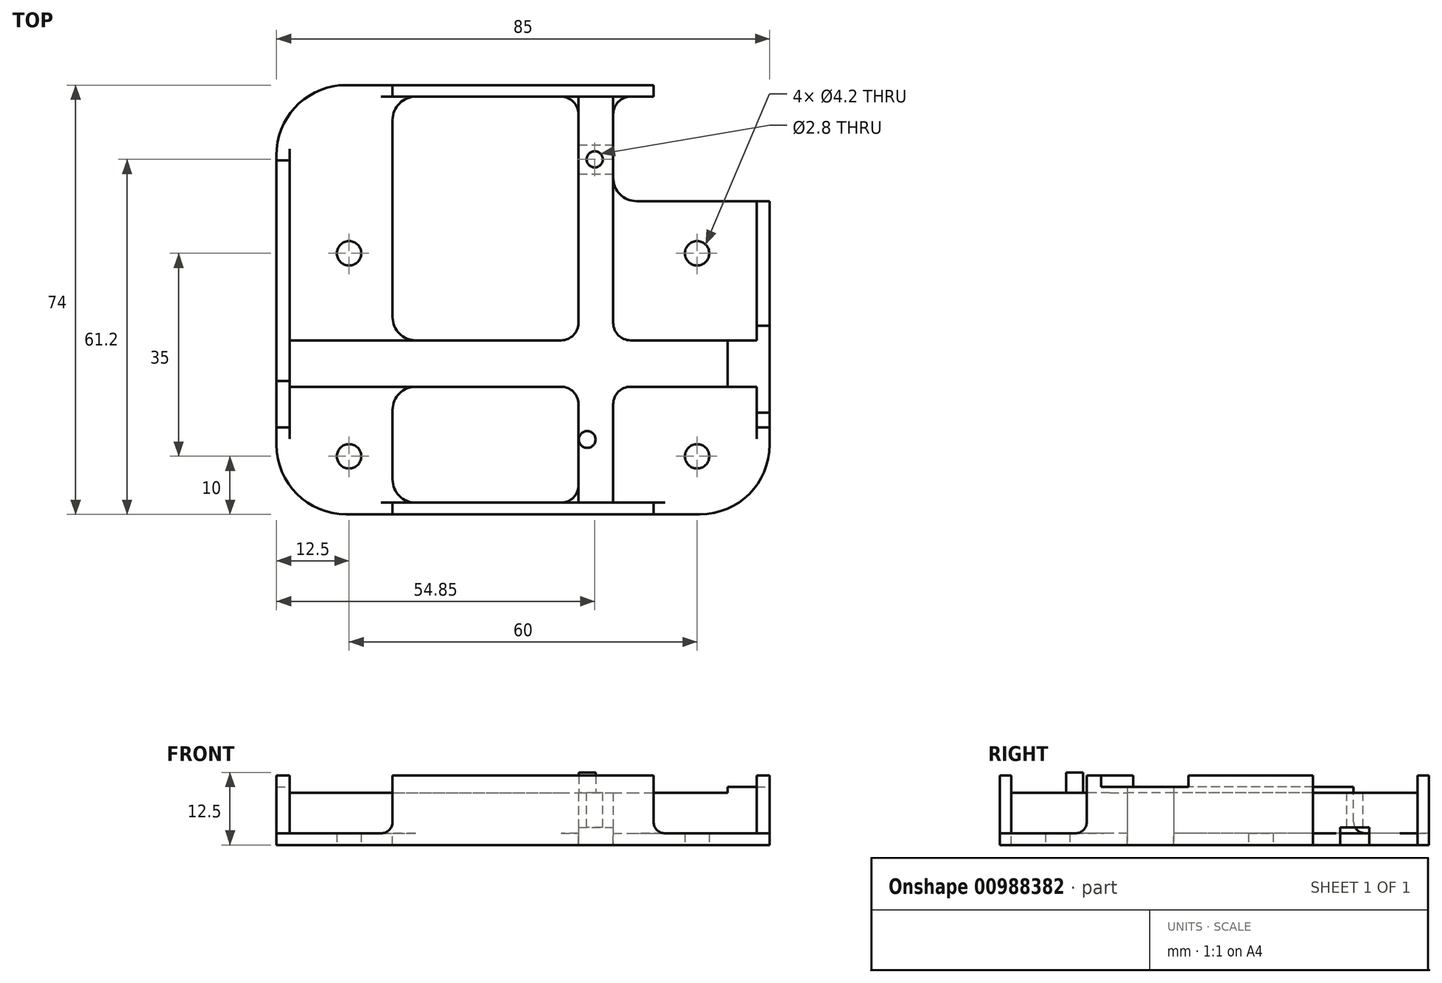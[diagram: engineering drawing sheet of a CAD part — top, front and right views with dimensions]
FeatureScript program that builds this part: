
annotation { "Feature Type Name" : "Feature", "Feature Type Description" : "" }
export const myFeature = defineFeature(function(context is Context, id is Id, definition is map)
    precondition{}
    {
        {
            var Q0;
            Q0=qCreatedBy(makeId("Top.planeOp"),FACE);
            var sketch = newSketch(context, id + "F0", { "sketchPlane" : qUnion([Q0])});
            skLineSegment(sketch, "E0.bottom", {"start": v(-42.5, 37) * mm, "end": v(42.5, 37) * mm});
            skLineSegment(sketch, "E0.top", {"start": v(-42.5, -37) * mm, "end": v(42.5, -37) * mm});
            skLineSegment(sketch, "E0.left", {"start": v(-42.5, 37) * mm, "end": v(-42.5, -37) * mm});
            skLineSegment(sketch, "E0.right", {"start": v(42.5, 37) * mm, "end": v(42.5, -37) * mm});
            skCircle(sketch, "E1", {"center": v(-30, 8) * mm, "radius": 2.1 * mm});
            skCircle(sketch, "E2", {"center": v(30, 8) * mm, "radius": 2.1 * mm});
            skCircle(sketch, "E3", {"center": v(30, -27) * mm, "radius": 2.1 * mm});
            skCircle(sketch, "E4", {"center": v(-30, -27) * mm, "radius": 2.1 * mm});
            skLineSegment(sketch, "E5.bottom", {"start": v(-30, 8) * mm, "end": v(30, 8) * mm, "construction": true});
            skLineSegment(sketch, "E5.top", {"start": v(-30, -27) * mm, "end": v(30, -27) * mm, "construction": true});
            skLineSegment(sketch, "E5.left", {"start": v(-30, 8) * mm, "end": v(-30, -27) * mm, "construction": true});
            skLineSegment(sketch, "E5.right", {"start": v(30, 8) * mm, "end": v(30, -27) * mm, "construction": true});
            skPoint(sketch, "E6", {"position": v(0, 8) * mm});
            skPoint(sketch, "E7", {"position": v(30, -9.5) * mm});
            skPoint(sketch, "E8", {"position": v(0, 37) * mm});
            skPoint(sketch, "E9", {"position": v(42.5, 0) * mm});
            skSolve(sketch);
        }
        {
            var Q0;
            Q0=makeQuery(id+"F0.imprint","IMPRINT",FACE,{"disambiguationData":[TD([[makeQuery(id+"F0.imprint","IMPRINT",EDGE,{"derivedFrom":sQuery(id+"F0.wireOp",EDGE,"E0.bottom")}),-1.0]])]});
            extrude(context, id + "F1", {"entities" : qUnion([Q0]), "depth" : 12 * mm, "offsetDistance" : 25 * mm});
        }
        {
            var Q0;
            Q0=makeQuery(id+"F1.opExtrude","CAP_FACE",FACE,{"disambiguationData":[OSD([sQuery(id+"F0.wireOp",EDGE,"E0.bottom"),sQuery(id+"F0.wireOp",EDGE,"E0.top"),sQuery(id+"F0.wireOp",EDGE,"E0.left"),sQuery(id+"F0.wireOp",EDGE,"E0.right"),sQuery(id+"F0.wireOp",EDGE,"E1"),sQuery(id+"F0.wireOp",EDGE,"E2"),sQuery(id+"F0.wireOp",EDGE,"E3"),sQuery(id+"F0.wireOp",EDGE,"E4")])],"isStart":false});
            var sketch = newSketch(context, id + "F2", { "sketchPlane" : qUnion([Q0])});
            skLineSegment(sketch, "E10.bottom", {"start": v(-40.25, 35) * mm, "end": v(40.25, 35) * mm});
            skLineSegment(sketch, "E10.top", {"start": v(-40.25, -35) * mm, "end": v(40.25, -35) * mm});
            skLineSegment(sketch, "E10.left", {"start": v(-40.25, 35) * mm, "end": v(-40.25, -35) * mm});
            skLineSegment(sketch, "E10.right", {"start": v(40.25, 35) * mm, "end": v(40.25, -35) * mm});
            skPoint(sketch, "E11", {"position": v(0, 35) * mm});
            skPoint(sketch, "E12", {"position": v(40.25, 0) * mm});
            skSolve(sketch);
        }
        {
            var Q0;
            Q0=makeQuery(id+"F2.imprint","IMPRINT",FACE,{"disambiguationData":[TD([[makeQuery(id+"F2.imprint","IMPRINT",EDGE,{"derivedFrom":sQuery(id+"F2.wireOp",EDGE,"E10.bottom")}),-1.0]])]});
            extrude(context, id + "F3", {"entities" : qUnion([Q0]), "operationType" : NewBodyOperationType.REMOVE, "oppositeDirection" : true, "depth" : 10 * mm, "offsetDistance" : 25 * mm});
        }
        {
            var Q0;
            Q0=makeQuery(id+"F3.boolean.opBoolean","COPY",FACE,{"derivedFrom":makeQuery(id+"F3.opExtrude","CAP_FACE",FACE,{"disambiguationData":[OSD([sQuery(id+"F0.wireOp",EDGE,"E1"),sQuery(id+"F0.wireOp",EDGE,"E2"),sQuery(id+"F0.wireOp",EDGE,"E3"),sQuery(id+"F0.wireOp",EDGE,"E4"),sQuery(id+"F2.wireOp",EDGE,"E10.bottom"),sQuery(id+"F2.wireOp",EDGE,"E10.top"),sQuery(id+"F2.wireOp",EDGE,"E10.left"),sQuery(id+"F2.wireOp",EDGE,"E10.right")])],"isStart":false})});
            var sketch = newSketch(context, id + "F4", { "sketchPlane" : qUnion([Q0])});
            skLineSegment(sketch, "E13.bottom", {"start": v(9.55, 35) * mm, "end": v(15.55, 35) * mm});
            skLineSegment(sketch, "E13.top", {"start": v(9.55, -35) * mm, "end": v(15.55, -35) * mm});
            skLineSegment(sketch, "E13.left", {"start": v(9.55, 35) * mm, "end": v(9.55, -35) * mm});
            skLineSegment(sketch, "E13.right", {"start": v(15.55, 35) * mm, "end": v(15.55, -35) * mm});
            skLineSegment(sketch, "E14.bottom", {"start": v(-40.25, -7) * mm, "end": v(40.25, -7) * mm});
            skLineSegment(sketch, "E14.top", {"start": v(-40.25, -15) * mm, "end": v(40.25, -15) * mm});
            skLineSegment(sketch, "E14.left", {"start": v(-40.25, -7) * mm, "end": v(-40.25, -15) * mm});
            skLineSegment(sketch, "E14.right", {"start": v(40.25, -7) * mm, "end": v(40.25, -15) * mm});
            skSolve(sketch);
        }
        {
            var Q0;
            Q0=makeQuery(id+"F4.imprint","IMPRINT",FACE,{"disambiguationData":[TD([[makeQuery(id+"F4.imprint","IMPRINT",EDGE,{"derivedFrom":sQuery(id+"F4.wireOp",EDGE,"E13.bottom")}),-1.0]])]});
            var Q1;
            {var subQ5=sQuery(id+"F4.wireOp",EDGE,"E14.left");Q1=makeQuery(id+"F4.imprint","IMPRINT",FACE,{"disambiguationData":[TD([[makeQuery(id+"F4.imprint","IMPRINT",EDGE,{"derivedFrom":subQ5}),1.0]])]});}
            var Q2;
            {var subQ0=sQuery(id+"F4.wireOp",EDGE,"E14.bottom");var subQ1=sQuery(id+"F4.wireOp",EDGE,"E13.left");var subQ2=makeQuery(id+"F4.imprint","INTERSECT",VERTEX,{"derivedFrom":[subQ1,subQ0]});Q2=makeQuery(id+"F4.imprint","IMPRINT",FACE,{"disambiguationData":[TD([[makeQuery(id+"F4.imprint","IMPRINT",EDGE,{"disambiguationData":[TD([[subQ2,-1.0]])],"derivedFrom":subQ1}),1.0]])]});}
            var Q3;
            {var subQ5=sQuery(id+"F4.wireOp",EDGE,"E14.right");Q3=makeQuery(id+"F4.imprint","IMPRINT",FACE,{"disambiguationData":[TD([[makeQuery(id+"F4.imprint","IMPRINT",EDGE,{"derivedFrom":subQ5}),-1.0]])]});}
            var Q4;
            {var subQ0=sQuery(id+"F4.wireOp",EDGE,"E13.top");Q4=makeQuery(id+"F4.imprint","IMPRINT",FACE,{"disambiguationData":[TD([[makeQuery(id+"F4.imprint","IMPRINT",EDGE,{"derivedFrom":subQ0}),1.0]])]});}
            extrude(context, id + "F5", {"entities" : qUnion([Q0, Q1, Q2, Q3, Q4]), "operationType" : NewBodyOperationType.ADD, "depth" : 7 * mm, "offsetDistance" : 25 * mm});
        }
        {
            var Q0;
            Q0=makeQuery(id+"F5.opExtrude","CAP_FACE",FACE,{"disambiguationData":[OSD([sQuery(id+"F4.wireOp",EDGE,"E13.bottom"),sQuery(id+"F4.wireOp",EDGE,"E13.top"),sQuery(id+"F4.wireOp",EDGE,"E13.left"),sQuery(id+"F4.wireOp",EDGE,"E13.right")])],"isStart":false});
            var sketch = newSketch(context, id + "F6", { "sketchPlane" : qUnion([Q0])});
            skCircle(sketch, "E15", {"center": v(12.35, 24.2) * mm, "radius": 1.4 * mm});
            skCircle(sketch, "E16", {"center": v(11.05, -24.1) * mm, "radius": 1.45 * mm});
            skSolve(sketch);
        }
        {
            var Q0;
            Q0=makeQuery(id+"F6.imprint","IMPRINT",FACE,{"disambiguationData":[TD([[makeQuery(id+"F6.imprint","IMPRINT",EDGE,{"derivedFrom":sQuery(id+"F6.wireOp",EDGE,"E16")}),1.0]])]});
            extrude(context, id + "F7", {"entities" : qUnion([Q0]), "operationType" : NewBodyOperationType.ADD, "depth" : 3.5 * mm, "offsetDistance" : 25 * mm});
        }
        {
            var Q0;
            Q0=makeQuery(id+"F1.opExtrude","CAP_FACE",FACE,{"disambiguationData":[OSD([sQuery(id+"F0.wireOp",EDGE,"E0.bottom"),sQuery(id+"F0.wireOp",EDGE,"E0.top"),sQuery(id+"F0.wireOp",EDGE,"E0.left"),sQuery(id+"F0.wireOp",EDGE,"E0.right"),sQuery(id+"F0.wireOp",EDGE,"E1"),sQuery(id+"F0.wireOp",EDGE,"E2"),sQuery(id+"F0.wireOp",EDGE,"E3"),sQuery(id+"F0.wireOp",EDGE,"E4")])],"isStart":false});
            var sketch = newSketch(context, id + "F8", { "sketchPlane" : qUnion([Q0])});
            skLineSegment(sketch, "E17.bottom", {"start": v(-42.5, 24) * mm, "end": v(-40.25, 24) * mm});
            skLineSegment(sketch, "E17.top", {"start": v(-42.5, -14) * mm, "end": v(-40.25, -14) * mm});
            skLineSegment(sketch, "E17.left", {"start": v(-42.5, 24) * mm, "end": v(-42.5, -14) * mm});
            skLineSegment(sketch, "E17.right", {"start": v(-40.25, 24) * mm, "end": v(-40.25, -14) * mm});
            skSolve(sketch);
        }
        {
            var Q0;
            Q0=makeQuery(id+"F8.imprint","IMPRINT",FACE,{"disambiguationData":[TD([[makeQuery(id+"F8.imprint","IMPRINT",EDGE,{"derivedFrom":sQuery(id+"F8.wireOp",EDGE,"E17.bottom")}),-1.0]])]});
            extrude(context, id + "F9", {"entities" : qUnion([Q0]), "operationType" : NewBodyOperationType.REMOVE, "oppositeDirection" : true, "depth" : 2 * mm, "offsetDistance" : 25 * mm});
        }
        {
            var Q0;
            Q0=makeQuery(id+"F1.opExtrude","CAP_FACE",FACE,{"disambiguationData":[OSD([sQuery(id+"F0.wireOp",EDGE,"E0.bottom"),sQuery(id+"F0.wireOp",EDGE,"E0.top"),sQuery(id+"F0.wireOp",EDGE,"E0.left"),sQuery(id+"F0.wireOp",EDGE,"E0.right"),sQuery(id+"F0.wireOp",EDGE,"E1"),sQuery(id+"F0.wireOp",EDGE,"E2"),sQuery(id+"F0.wireOp",EDGE,"E3"),sQuery(id+"F0.wireOp",EDGE,"E4")])],"isStart":false});
            var sketch = newSketch(context, id + "F10", { "sketchPlane" : qUnion([Q0])});
            skLineSegment(sketch, "E18", {"start": v(-42.5, 17) * mm, "end": v(-42.5, 37) * mm});
            skLineSegment(sketch, "E19", {"start": v(-42.5, 37) * mm, "end": v(-22.5, 37) * mm});
            skLineSegment(sketch, "E20", {"start": v(-22.5, 37) * mm, "end": v(-22.5, 35) * mm});
            skLineSegment(sketch, "E21", {"start": v(-22.5, 35) * mm, "end": v(-40.25, 35) * mm});
            skLineSegment(sketch, "E22", {"start": v(-40.25, 35) * mm, "end": v(-40.25, 17) * mm});
            skLineSegment(sketch, "E23", {"start": v(-40.25, 17) * mm, "end": v(-42.5, 17) * mm});
            skLineSegment(sketch, "E24", {"start": v(22.5, 37) * mm, "end": v(22.5, 35) * mm});
            skLineSegment(sketch, "E25", {"start": v(22.5, 35) * mm, "end": v(40.25, 35) * mm});
            skLineSegment(sketch, "E26", {"start": v(40.25, 35) * mm, "end": v(40.25, 17) * mm});
            skLineSegment(sketch, "E27", {"start": v(40.25, 17) * mm, "end": v(42.5, 17) * mm});
            skLineSegment(sketch, "E28", {"start": v(42.5, 17) * mm, "end": v(42.5, 37) * mm});
            skLineSegment(sketch, "E29", {"start": v(42.5, 37) * mm, "end": v(22.5, 37) * mm});
            skLineSegment(sketch, "E30", {"start": v(22.5, -35) * mm, "end": v(22.5, -37) * mm});
            skLineSegment(sketch, "E31", {"start": v(22.5, -37) * mm, "end": v(42.5, -37) * mm});
            skLineSegment(sketch, "E32", {"start": v(42.5, -37) * mm, "end": v(42.5, -22) * mm});
            skLineSegment(sketch, "E33", {"start": v(42.5, -22) * mm, "end": v(40.25, -22) * mm});
            skLineSegment(sketch, "E34", {"start": v(40.25, -22) * mm, "end": v(40.25, -35) * mm});
            skLineSegment(sketch, "E35", {"start": v(40.25, -35) * mm, "end": v(22.5, -35) * mm});
            skLineSegment(sketch, "E36", {"start": v(-42.5, -22) * mm, "end": v(-40.25, -22) * mm});
            skLineSegment(sketch, "E37", {"start": v(-40.25, -22) * mm, "end": v(-40.25, -35) * mm});
            skLineSegment(sketch, "E38", {"start": v(-40.25, -35) * mm, "end": v(-22.5, -35) * mm});
            skLineSegment(sketch, "E39", {"start": v(-22.5, -35) * mm, "end": v(-22.5, -37) * mm});
            skLineSegment(sketch, "E40", {"start": v(-22.5, -37) * mm, "end": v(-42.5, -37) * mm});
            skLineSegment(sketch, "E41", {"start": v(-42.5, -37) * mm, "end": v(-42.5, -22) * mm});
            skSolve(sketch);
        }
        {
            var Q0;
            Q0=makeQuery(id+"F10.imprint","IMPRINT",FACE,{"disambiguationData":[TD([[makeQuery(id+"F10.imprint","IMPRINT",EDGE,{"derivedFrom":sQuery(id+"F10.wireOp",EDGE,"E18")}),1.0]])]});
            var Q1;
            Q1=makeQuery(id+"F10.imprint","IMPRINT",FACE,{"disambiguationData":[TD([[makeQuery(id+"F10.imprint","IMPRINT",EDGE,{"derivedFrom":sQuery(id+"F10.wireOp",EDGE,"E24")}),1.0]])]});
            var Q2;
            Q2=makeQuery(id+"F10.imprint","IMPRINT",FACE,{"disambiguationData":[TD([[makeQuery(id+"F10.imprint","IMPRINT",EDGE,{"derivedFrom":sQuery(id+"F10.wireOp",EDGE,"E30")}),1.0]])]});
            var Q3;
            Q3=makeQuery(id+"F10.imprint","IMPRINT",FACE,{"disambiguationData":[TD([[makeQuery(id+"F10.imprint","IMPRINT",EDGE,{"derivedFrom":sQuery(id+"F10.wireOp",EDGE,"E36")}),-1.0]])]});
            var Q4;
            {var subQ0=sQuery(id+"F2.wireOp",EDGE,"E10.left");var subQ1=sQuery(id+"F2.wireOp",EDGE,"E10.bottom");var subQ5=sQuery(id+"F0.wireOp",EDGE,"E1");Q4=makeQuery(id+"F5.boolean.opBoolean","SPLIT",FACE,{"disambiguationData":[TD([makeQuery(id+"F1.opExtrude","SWEPT_FACE",FACE,{"disambiguationData":[OSD([subQ5])]})])],"derivedFrom":makeQuery(id+"F3.boolean.opBoolean","COPY",FACE,{"derivedFrom":makeQuery(id+"F3.opExtrude","CAP_FACE",FACE,{"disambiguationData":[OSD([subQ5,sQuery(id+"F0.wireOp",EDGE,"E2"),sQuery(id+"F0.wireOp",EDGE,"E3"),sQuery(id+"F0.wireOp",EDGE,"E4"),subQ1,sQuery(id+"F2.wireOp",EDGE,"E10.top"),subQ0,sQuery(id+"F2.wireOp",EDGE,"E10.right")])],"isStart":false})})});}
            extrude(context, id + "F11", {"entities" : qUnion([Q0, Q1, Q2, Q3]), "operationType" : NewBodyOperationType.REMOVE, "endBound" : BoundingType.UP_TO_SURFACE, "oppositeDirection" : true, "depth" : 25 * mm, "endBoundEntityFace" : qUnion([Q4]), "offsetDistance" : 25 * mm});
        }
        {
            var Q0;
            {var subQ0=sQuery(id+"F0.wireOp",EDGE,"E0.right");Q0=makeQuery(id+"F11.boolean.opBoolean","SPLIT",FACE,{"disambiguationData":[TD([makeQuery(id+"F1.opExtrude","SWEPT_FACE",FACE,{"disambiguationData":[OSD([subQ0])]})])],"derivedFrom":makeQuery(id+"F1.opExtrude","CAP_FACE",FACE,{"disambiguationData":[OSD([sQuery(id+"F0.wireOp",EDGE,"E0.bottom"),sQuery(id+"F0.wireOp",EDGE,"E0.top"),sQuery(id+"F0.wireOp",EDGE,"E0.left"),subQ0,sQuery(id+"F0.wireOp",EDGE,"E1"),sQuery(id+"F0.wireOp",EDGE,"E2"),sQuery(id+"F0.wireOp",EDGE,"E3"),sQuery(id+"F0.wireOp",EDGE,"E4")])],"isStart":false})});}
            var sketch = newSketch(context, id + "F12", { "sketchPlane" : qUnion([Q0])});
            skLineSegment(sketch, "E42.bottom", {"start": v(40.25, -4.5) * mm, "end": v(42.5, -4.5) * mm});
            skLineSegment(sketch, "E42.top", {"start": v(40.25, -19.5) * mm, "end": v(42.5, -19.5) * mm});
            skLineSegment(sketch, "E42.left", {"start": v(40.25, -4.5) * mm, "end": v(40.25, -19.5) * mm});
            skLineSegment(sketch, "E42.right", {"start": v(42.5, -4.5) * mm, "end": v(42.5, -19.5) * mm});
            skPoint(sketch, "E43", {"position": v(42.5, -12) * mm});
            skSolve(sketch);
        }
        {
            var Q0;
            Q0=makeQuery(id+"F12.imprint","IMPRINT",FACE,{"disambiguationData":[TD([[makeQuery(id+"F12.imprint","IMPRINT",EDGE,{"derivedFrom":sQuery(id+"F12.wireOp",EDGE,"E42.bottom")}),-1.0]])]});
            var Q1;
            Q1=makeQuery(id+"F9.boolean.opBoolean","MERGE",FACE,{"derivedFrom":[makeQuery(id+"F5.opExtrude","CAP_FACE",FACE,{"disambiguationData":[OSD([sQuery(id+"F4.wireOp",EDGE,"E13.bottom"),sQuery(id+"F4.wireOp",EDGE,"E13.top"),sQuery(id+"F4.wireOp",EDGE,"E13.left"),sQuery(id+"F4.wireOp",EDGE,"E13.right"),sQuery(id+"F4.wireOp",EDGE,"E14.bottom"),sQuery(id+"F4.wireOp",EDGE,"E14.top"),sQuery(id+"F4.wireOp",EDGE,"E14.left"),sQuery(id+"F4.wireOp",EDGE,"E14.right")])],"isStart":false})],"fromTools":[makeQuery(id+"F9.opExtrude","CAP_FACE",FACE,{"disambiguationData":[OSD([sQuery(id+"F8.wireOp",EDGE,"E17.bottom"),sQuery(id+"F8.wireOp",EDGE,"E17.top"),sQuery(id+"F8.wireOp",EDGE,"E17.left"),sQuery(id+"F8.wireOp",EDGE,"E17.right")])],"isStart":false})]});
            extrude(context, id + "F13", {"entities" : qUnion([Q0]), "operationType" : NewBodyOperationType.REMOVE, "oppositeDirection" : true, "depth" : 2 * mm, "endBoundEntityFace" : qUnion([Q1]), "offsetDistance" : 25 * mm});
        }
        {
            var Q0;
            Q0=makeQuery(id+"F1.opExtrude","SWEPT_EDGE",EDGE,{"disambiguationData":[OSD([sQuery(id+"F0.wireOp",EDGE,"E0.bottom"),sQuery(id+"F0.wireOp",EDGE,"E0.left")])]});
            var Q1;
            Q1=makeQuery(id+"F1.opExtrude","SWEPT_EDGE",EDGE,{"disambiguationData":[OSD([sQuery(id+"F0.wireOp",EDGE,"E0.top"),sQuery(id+"F0.wireOp",EDGE,"E0.left")])]});
            var Q2;
            Q2=makeQuery(id+"F1.opExtrude","SWEPT_EDGE",EDGE,{"disambiguationData":[OSD([sQuery(id+"F0.wireOp",EDGE,"E0.top"),sQuery(id+"F0.wireOp",EDGE,"E0.right")])]});
            var Q3;
            Q3=makeQuery(id+"F1.opExtrude","SWEPT_EDGE",EDGE,{"disambiguationData":[OSD([sQuery(id+"F0.wireOp",EDGE,"E0.bottom"),sQuery(id+"F0.wireOp",EDGE,"E0.right")])]});
            fillet(context, id + "F14", {"entities" : qUnion([Q0, Q1, Q2, Q3]), "radius" : 12 * mm, "tangentPropagation" : true, "allowEdgeOverflow" : false});
        }
        {
            var Q0;
            Q0=makeQuery(id+"F5.opExtrude","SWEPT_EDGE",EDGE,{"disambiguationData":[OSD([sQuery(id+"F4.wireOp",EDGE,"E13.left"),sQuery(id+"F4.wireOp",EDGE,"E14.bottom")])]});
            var Q1;
            Q1=makeQuery(id+"F5.opExtrude","SWEPT_EDGE",EDGE,{"disambiguationData":[OSD([sQuery(id+"F4.wireOp",EDGE,"E13.left"),sQuery(id+"F4.wireOp",EDGE,"E14.top")])]});
            var Q2;
            Q2=makeQuery(id+"F5.opExtrude","SWEPT_EDGE",EDGE,{"disambiguationData":[OSD([sQuery(id+"F4.wireOp",EDGE,"E13.right"),sQuery(id+"F4.wireOp",EDGE,"E14.top")])]});
            var Q3;
            Q3=makeQuery(id+"F5.opExtrude","SWEPT_EDGE",EDGE,{"disambiguationData":[OSD([sQuery(id+"F4.wireOp",EDGE,"E13.right"),sQuery(id+"F4.wireOp",EDGE,"E14.bottom")])]});
            var Q4;
            Q4=makeQuery(id+"F5.opExtrude","SWEPT_EDGE",EDGE,{"disambiguationData":[OSD([sQuery(id+"F2.wireOp",EDGE,"E10.left"),sQuery(id+"F4.wireOp",EDGE,"E14.bottom"),sQuery(id+"F4.wireOp",EDGE,"E14.left")])]});
            var Q5;
            Q5=makeQuery(id+"F5.opExtrude","SWEPT_EDGE",EDGE,{"disambiguationData":[OSD([sQuery(id+"F2.wireOp",EDGE,"E10.left"),sQuery(id+"F4.wireOp",EDGE,"E14.top"),sQuery(id+"F4.wireOp",EDGE,"E14.left")])]});
            var Q6;
            Q6=makeQuery(id+"F5.opExtrude","SWEPT_EDGE",EDGE,{"disambiguationData":[OSD([sQuery(id+"F2.wireOp",EDGE,"E10.bottom"),sQuery(id+"F4.wireOp",EDGE,"E13.bottom"),sQuery(id+"F4.wireOp",EDGE,"E13.left")])]});
            var Q7;
            Q7=makeQuery(id+"F5.opExtrude","SWEPT_EDGE",EDGE,{"disambiguationData":[OSD([sQuery(id+"F2.wireOp",EDGE,"E10.bottom"),sQuery(id+"F4.wireOp",EDGE,"E13.bottom"),sQuery(id+"F4.wireOp",EDGE,"E13.right")])]});
            var Q8;
            Q8=makeQuery(id+"F5.opExtrude","SWEPT_EDGE",EDGE,{"disambiguationData":[OSD([sQuery(id+"F2.wireOp",EDGE,"E10.top"),sQuery(id+"F4.wireOp",EDGE,"E13.top"),sQuery(id+"F4.wireOp",EDGE,"E13.left")])]});
            var Q9;
            Q9=makeQuery(id+"F5.opExtrude","SWEPT_EDGE",EDGE,{"disambiguationData":[OSD([sQuery(id+"F2.wireOp",EDGE,"E10.right"),sQuery(id+"F4.wireOp",EDGE,"E14.top"),sQuery(id+"F4.wireOp",EDGE,"E14.right")])]});
            var Q10;
            Q10=makeQuery(id+"F5.opExtrude","SWEPT_EDGE",EDGE,{"disambiguationData":[OSD([sQuery(id+"F2.wireOp",EDGE,"E10.top"),sQuery(id+"F4.wireOp",EDGE,"E13.top"),sQuery(id+"F4.wireOp",EDGE,"E13.right")])]});
            fillet(context, id + "F15", {"entities" : qUnion([Q0, Q1, Q2, Q3, Q4, Q5, Q6, Q7, Q8, Q9, Q10]), "radius" : 3 * mm, "tangentPropagation" : true, "allowEdgeOverflow" : false});
        }
        {
            var Q0;
            {var subQ1=sQuery(id+"F2.wireOp",EDGE,"E10.top");var subQ4=sQuery(id+"F2.wireOp",EDGE,"E10.left");var subQ5=sQuery(id+"F0.wireOp",EDGE,"E4");Q0=makeQuery(id+"F11.boolean.opBoolean","MERGE",FACE,{"derivedFrom":[makeQuery(id+"F5.boolean.opBoolean","SPLIT",FACE,{"disambiguationData":[TD([makeQuery(id+"F1.opExtrude","SWEPT_FACE",FACE,{"disambiguationData":[OSD([subQ5])]})])],"derivedFrom":makeQuery(id+"F3.boolean.opBoolean","COPY",FACE,{"derivedFrom":makeQuery(id+"F3.opExtrude","CAP_FACE",FACE,{"disambiguationData":[OSD([sQuery(id+"F0.wireOp",EDGE,"E1"),sQuery(id+"F0.wireOp",EDGE,"E2"),sQuery(id+"F0.wireOp",EDGE,"E3"),subQ5,sQuery(id+"F2.wireOp",EDGE,"E10.bottom"),subQ1,subQ4,sQuery(id+"F2.wireOp",EDGE,"E10.right")])],"isStart":false})})})],"fromTools":[makeQuery(id+"F11.opExtrude","CAP_FACE",FACE,{"disambiguationData":[OSD([sQuery(id+"F10.wireOp",EDGE,"E36"),sQuery(id+"F10.wireOp",EDGE,"E37"),sQuery(id+"F10.wireOp",EDGE,"E38"),sQuery(id+"F10.wireOp",EDGE,"E39"),sQuery(id+"F10.wireOp",EDGE,"E40"),sQuery(id+"F10.wireOp",EDGE,"E41")])],"isStart":false})]});}
            var sketch = newSketch(context, id + "F16", { "sketchPlane" : qUnion([Q0])});
            skLineSegment(sketch, "E44.0.0", {"start": v(6.55, -15) * mm, "end": v(-37.25, -15) * mm});
            skArc(sketch, "E44.0.1", {"start": v(-37.25, -15) * mm, "mid": v(-39.37, -15.88) * mm, "end": v(-40.25, -18) * mm});
            skLineSegment(sketch, "E44.0.2", {"start": v(-40.25, -18) * mm, "end": v(-40.25, -22) * mm});
            skLineSegment(sketch, "E44.0.3", {"start": v(-40.25, -22) * mm, "end": v(-42.5, -22) * mm});
            skLineSegment(sketch, "E44.0.4", {"start": v(-42.5, -22) * mm, "end": v(-42.5, -25) * mm});
            skArc(sketch, "E44.0.5", {"start": v(-42.5, -25) * mm, "mid": v(-38.99, -33.49) * mm, "end": v(-30.5, -37) * mm});
            skLineSegment(sketch, "E44.0.6", {"start": v(-30.5, -37) * mm, "end": v(-22.5, -37) * mm});
            skLineSegment(sketch, "E44.0.7", {"start": v(-22.5, -37) * mm, "end": v(-22.5, -35) * mm});
            skLineSegment(sketch, "E44.0.8", {"start": v(-22.5, -35) * mm, "end": v(6.55, -35) * mm});
            skArc(sketch, "E44.0.9", {"start": v(6.55, -35) * mm, "mid": v(8.67, -34.12) * mm, "end": v(9.55, -32) * mm});
            skLineSegment(sketch, "E44.0.10", {"start": v(9.55, -32) * mm, "end": v(9.55, -18) * mm});
            skArc(sketch, "E44.0.11", {"start": v(9.55, -18) * mm, "mid": v(8.67, -15.88) * mm, "end": v(6.55, -15) * mm});
            skLineSegment(sketch, "E45", {"start": v(-22.5, -35) * mm, "end": v(-22.5, -15) * mm});
            skSolve(sketch);
        }
        {
            var Q0;
            Q0=makeQuery(id+"F16.imprint","IMPRINT",FACE,{"disambiguationData":[TD([[makeQuery(id+"F16.imprint","IMPRINT",EDGE,{"derivedFrom":sQuery(id+"F16.wireOp",EDGE,"E44.0.8")}),1.0]])]});
            extrude(context, id + "F17", {"entities" : qUnion([Q0]), "operationType" : NewBodyOperationType.REMOVE, "endBound" : BoundingType.UP_TO_NEXT, "oppositeDirection" : true, "depth" : 25 * mm, "offsetDistance" : 25 * mm});
        }
        {
            var Q0;
            {var subQ0=sQuery(id+"F2.wireOp",EDGE,"E10.left");var subQ1=sQuery(id+"F2.wireOp",EDGE,"E10.bottom");var subQ5=sQuery(id+"F0.wireOp",EDGE,"E1");Q0=makeQuery(id+"F11.boolean.opBoolean","MERGE",FACE,{"derivedFrom":[makeQuery(id+"F5.boolean.opBoolean","SPLIT",FACE,{"disambiguationData":[TD([makeQuery(id+"F1.opExtrude","SWEPT_FACE",FACE,{"disambiguationData":[OSD([subQ5])]})])],"derivedFrom":makeQuery(id+"F3.boolean.opBoolean","COPY",FACE,{"derivedFrom":makeQuery(id+"F3.opExtrude","CAP_FACE",FACE,{"disambiguationData":[OSD([subQ5,sQuery(id+"F0.wireOp",EDGE,"E2"),sQuery(id+"F0.wireOp",EDGE,"E3"),sQuery(id+"F0.wireOp",EDGE,"E4"),subQ1,sQuery(id+"F2.wireOp",EDGE,"E10.top"),subQ0,sQuery(id+"F2.wireOp",EDGE,"E10.right")])],"isStart":false})})})],"fromTools":[makeQuery(id+"F11.opExtrude","CAP_FACE",FACE,{"disambiguationData":[OSD([sQuery(id+"F8.wireOp",EDGE,"E17.bottom"),sQuery(id+"F10.wireOp",EDGE,"E18"),sQuery(id+"F10.wireOp",EDGE,"E19"),sQuery(id+"F10.wireOp",EDGE,"E20"),sQuery(id+"F10.wireOp",EDGE,"E21"),sQuery(id+"F10.wireOp",EDGE,"E22")])],"isStart":false})]});}
            var sketch = newSketch(context, id + "F18", { "sketchPlane" : qUnion([Q0])});
            skLineSegment(sketch, "E46.0.0", {"start": v(-37.25, -7) * mm, "end": v(6.55, -7) * mm});
            skArc(sketch, "E46.0.1", {"start": v(6.55, -7) * mm, "mid": v(8.67, -6.12) * mm, "end": v(9.55, -4) * mm});
            skLineSegment(sketch, "E46.0.2", {"start": v(9.55, -4) * mm, "end": v(9.55, 32) * mm});
            skArc(sketch, "E46.0.3", {"start": v(9.55, 32) * mm, "mid": v(8.67, 34.12) * mm, "end": v(6.55, 35) * mm});
            skLineSegment(sketch, "E46.0.4", {"start": v(6.55, 35) * mm, "end": v(-22.5, 35) * mm});
            skLineSegment(sketch, "E46.0.5", {"start": v(-22.5, 35) * mm, "end": v(-22.5, 37) * mm});
            skLineSegment(sketch, "E46.0.6", {"start": v(-22.5, 37) * mm, "end": v(-30.5, 37) * mm});
            skArc(sketch, "E46.0.7", {"start": v(-30.5, 37) * mm, "mid": v(-38.99, 33.49) * mm, "end": v(-42.5, 25) * mm});
            skLineSegment(sketch, "E46.0.8", {"start": v(-42.5, 25) * mm, "end": v(-42.5, 24) * mm});
            skLineSegment(sketch, "E46.0.9", {"start": v(-42.5, 24) * mm, "end": v(-40.25, 24) * mm});
            skLineSegment(sketch, "E46.0.10", {"start": v(-40.25, 24) * mm, "end": v(-40.25, -4) * mm});
            skArc(sketch, "E46.0.11", {"start": v(-40.25, -4) * mm, "mid": v(-39.37, -6.12) * mm, "end": v(-37.25, -7) * mm});
            skLineSegment(sketch, "E47", {"start": v(-22.5, 35) * mm, "end": v(-22.5, -7) * mm});
            skSolve(sketch);
        }
        {
            var Q0;
            {var subQ0=sQuery(id+"F18.wireOp",EDGE,"E46.0.1");Q0=makeQuery(id+"F18.imprint","IMPRINT",FACE,{"disambiguationData":[TD([[makeQuery(id+"F18.imprint","IMPRINT",EDGE,{"derivedFrom":subQ0}),1.0]])]});}
            extrude(context, id + "F19", {"entities" : qUnion([Q0]), "operationType" : NewBodyOperationType.REMOVE, "endBound" : BoundingType.UP_TO_NEXT, "oppositeDirection" : true, "depth" : 25 * mm, "offsetDistance" : 25 * mm});
        }
        {
            var Q0;
            {var subQ1=sQuery(id+"F2.wireOp",EDGE,"E10.bottom");var subQ4=sQuery(id+"F2.wireOp",EDGE,"E10.right");var subQ5=sQuery(id+"F0.wireOp",EDGE,"E2");Q0=makeQuery(id+"F11.boolean.opBoolean","MERGE",FACE,{"derivedFrom":[makeQuery(id+"F5.boolean.opBoolean","SPLIT",FACE,{"disambiguationData":[TD([makeQuery(id+"F1.opExtrude","SWEPT_FACE",FACE,{"disambiguationData":[OSD([subQ5])]})])],"derivedFrom":makeQuery(id+"F3.boolean.opBoolean","COPY",FACE,{"derivedFrom":makeQuery(id+"F3.opExtrude","CAP_FACE",FACE,{"disambiguationData":[OSD([sQuery(id+"F0.wireOp",EDGE,"E1"),subQ5,sQuery(id+"F0.wireOp",EDGE,"E3"),sQuery(id+"F0.wireOp",EDGE,"E4"),subQ1,sQuery(id+"F2.wireOp",EDGE,"E10.top"),sQuery(id+"F2.wireOp",EDGE,"E10.left"),subQ4])],"isStart":false})})})],"fromTools":[makeQuery(id+"F11.opExtrude","CAP_FACE",FACE,{"disambiguationData":[OSD([sQuery(id+"F10.wireOp",EDGE,"E24"),sQuery(id+"F10.wireOp",EDGE,"E25"),sQuery(id+"F10.wireOp",EDGE,"E26"),sQuery(id+"F10.wireOp",EDGE,"E27"),sQuery(id+"F10.wireOp",EDGE,"E28"),sQuery(id+"F10.wireOp",EDGE,"E29")])],"isStart":false})]});}
            var sketch = newSketch(context, id + "F20", { "sketchPlane" : qUnion([Q0])});
            skLineSegment(sketch, "E48.0.0", {"start": v(15.55, 32) * mm, "end": v(15.55, -4) * mm});
            skArc(sketch, "E48.0.1", {"start": v(15.55, -4) * mm, "mid": v(16.43, -6.12) * mm, "end": v(18.55, -7) * mm});
            skLineSegment(sketch, "E48.0.2", {"start": v(18.55, -7) * mm, "end": v(40.25, -7) * mm});
            skLineSegment(sketch, "E48.0.3", {"start": v(40.25, -7) * mm, "end": v(40.25, 17) * mm});
            skLineSegment(sketch, "E48.0.4", {"start": v(40.25, 17) * mm, "end": v(42.5, 17) * mm});
            skLineSegment(sketch, "E48.0.5", {"start": v(42.5, 17) * mm, "end": v(42.5, 25) * mm});
            skArc(sketch, "E48.0.6", {"start": v(42.5, 25) * mm, "mid": v(38.99, 33.49) * mm, "end": v(30.5, 37) * mm});
            skLineSegment(sketch, "E48.0.7", {"start": v(30.5, 37) * mm, "end": v(22.5, 37) * mm});
            skLineSegment(sketch, "E48.0.8", {"start": v(22.5, 37) * mm, "end": v(22.5, 35) * mm});
            skLineSegment(sketch, "E48.0.9", {"start": v(22.5, 35) * mm, "end": v(18.55, 35) * mm});
            skArc(sketch, "E48.0.10", {"start": v(18.55, 35) * mm, "mid": v(16.43, 34.12) * mm, "end": v(15.55, 32) * mm});
            skLineSegment(sketch, "E49", {"start": v(40.25, 17) * mm, "end": v(15.55, 17) * mm});
            skSolve(sketch);
        }
        {
            var Q0;
            Q0=makeQuery(id+"F20.imprint","IMPRINT",FACE,{"disambiguationData":[TD([[makeQuery(id+"F20.imprint","IMPRINT",EDGE,{"derivedFrom":sQuery(id+"F20.wireOp",EDGE,"E48.0.4")}),-1.0]])]});
            extrude(context, id + "F21", {"entities" : qUnion([Q0]), "operationType" : NewBodyOperationType.REMOVE, "endBound" : BoundingType.UP_TO_NEXT, "oppositeDirection" : true, "depth" : 25 * mm, "offsetDistance" : 25 * mm});
        }
        {
            var Q0;
            Q0=makeQuery(id+"F19.boolean.opBoolean","COPY",EDGE,{"derivedFrom":makeQuery(id+"F19.opExtrude","SWEPT_EDGE",EDGE,{"disambiguationData":[OSD([sQuery(id+"F18.wireOp",EDGE,"E46.0.4"),sQuery(id+"F18.wireOp",EDGE,"E46.0.5"),sQuery(id+"F18.wireOp",EDGE,"E47")])]})});
            var Q1;
            Q1=makeQuery(id+"F19.boolean.opBoolean","COPY",EDGE,{"derivedFrom":makeQuery(id+"F19.opExtrude","SWEPT_EDGE",EDGE,{"disambiguationData":[OSD([sQuery(id+"F18.wireOp",EDGE,"E46.0.0"),sQuery(id+"F18.wireOp",EDGE,"E47")])]})});
            var Q2;
            Q2=makeQuery(id+"F21.boolean.opBoolean","COPY",EDGE,{"derivedFrom":makeQuery(id+"F21.opExtrude","SWEPT_EDGE",EDGE,{"disambiguationData":[OSD([sQuery(id+"F20.wireOp",EDGE,"E48.0.0"),sQuery(id+"F20.wireOp",EDGE,"E49")])]})});
            var Q3;
            Q3=makeQuery(id+"F17.boolean.opBoolean","COPY",EDGE,{"derivedFrom":makeQuery(id+"F17.opExtrude","SWEPT_EDGE",EDGE,{"disambiguationData":[OSD([sQuery(id+"F16.wireOp",EDGE,"E44.0.0"),sQuery(id+"F16.wireOp",EDGE,"E45")])]})});
            var Q4;
            Q4=makeQuery(id+"F17.boolean.opBoolean","COPY",EDGE,{"derivedFrom":makeQuery(id+"F17.opExtrude","SWEPT_EDGE",EDGE,{"disambiguationData":[OSD([sQuery(id+"F16.wireOp",EDGE,"E44.0.7"),sQuery(id+"F16.wireOp",EDGE,"E44.0.8"),sQuery(id+"F16.wireOp",EDGE,"E45")])]})});
            fillet(context, id + "F22", {"entities" : qUnion([Q0, Q1, Q2, Q3, Q4]), "radius" : 4 * mm, "tangentPropagation" : true, "allowEdgeOverflow" : false});
        }
        {
            var Q0;
            Q0=makeQuery(id+"F11.boolean.opBoolean","COPY",EDGE,{"derivedFrom":makeQuery(id+"F11.opExtrude","CAP_EDGE",EDGE,{"disambiguationData":[OSD([sQuery(id+"F10.wireOp",EDGE,"E39")])],"isStart":true})});
            var Q1;
            Q1=makeQuery(id+"F11.boolean.opBoolean","COPY",EDGE,{"derivedFrom":makeQuery(id+"F11.opExtrude","CAP_EDGE",EDGE,{"disambiguationData":[OSD([sQuery(id+"F10.wireOp",EDGE,"E30")])],"isStart":true})});
            var Q2;
            Q2=makeQuery(id+"F11.boolean.opBoolean","COPY",EDGE,{"derivedFrom":makeQuery(id+"F11.opExtrude","CAP_EDGE",EDGE,{"disambiguationData":[OSD([sQuery(id+"F10.wireOp",EDGE,"E36")])],"isStart":true})});
            var Q3;
            Q3=makeQuery(id+"F11.boolean.opBoolean","COPY",EDGE,{"derivedFrom":makeQuery(id+"F11.opExtrude","CAP_EDGE",EDGE,{"disambiguationData":[OSD([sQuery(id+"F10.wireOp",EDGE,"E20")])],"isStart":true})});
            var Q4;
            Q4=makeQuery(id+"F11.boolean.opBoolean","COPY",EDGE,{"derivedFrom":makeQuery(id+"F11.opExtrude","CAP_EDGE",EDGE,{"disambiguationData":[OSD([sQuery(id+"F10.wireOp",EDGE,"E20")])],"isStart":false})});
            var Q5;
            Q5=makeQuery(id+"F11.boolean.opBoolean","COPY",EDGE,{"derivedFrom":makeQuery(id+"F11.opExtrude","CAP_EDGE",EDGE,{"disambiguationData":[OSD([sQuery(id+"F10.wireOp",EDGE,"E24")])],"isStart":true})});
            var Q6;
            Q6=makeQuery(id+"F11.boolean.opBoolean","COPY",EDGE,{"derivedFrom":makeQuery(id+"F11.opExtrude","CAP_EDGE",EDGE,{"disambiguationData":[OSD([sQuery(id+"F10.wireOp",EDGE,"E27")])],"isStart":true})});
            var Q7;
            Q7=makeQuery(id+"F9.boolean.opBoolean","COPY",EDGE,{"derivedFrom":makeQuery(id+"F9.opExtrude","CAP_EDGE",EDGE,{"disambiguationData":[OSD([sQuery(id+"F8.wireOp",EDGE,"E17.bottom")])],"isStart":false})});
            var Q8;
            Q8=makeQuery(id+"F11.boolean.opBoolean","COPY",EDGE,{"derivedFrom":makeQuery(id+"F11.opExtrude","CAP_EDGE",EDGE,{"disambiguationData":[OSD([sQuery(id+"F10.wireOp",EDGE,"E39")])],"isStart":false})});
            var Q9;
            Q9=makeQuery(id+"F11.boolean.opBoolean","COPY",EDGE,{"derivedFrom":makeQuery(id+"F11.opExtrude","CAP_EDGE",EDGE,{"disambiguationData":[OSD([sQuery(id+"F10.wireOp",EDGE,"E30")])],"isStart":false})});
            var Q10;
            Q10=makeQuery(id+"F11.boolean.opBoolean","COPY",EDGE,{"derivedFrom":makeQuery(id+"F11.opExtrude","CAP_EDGE",EDGE,{"disambiguationData":[OSD([sQuery(id+"F10.wireOp",EDGE,"E33")])],"isStart":false})});
            var Q11;
            Q11=makeQuery(id+"F11.boolean.opBoolean","COPY",EDGE,{"derivedFrom":makeQuery(id+"F11.opExtrude","CAP_EDGE",EDGE,{"disambiguationData":[OSD([sQuery(id+"F10.wireOp",EDGE,"E36")])],"isStart":false})});
            var Q12;
            Q12=makeQuery(id+"F11.boolean.opBoolean","COPY",EDGE,{"derivedFrom":makeQuery(id+"F11.opExtrude","CAP_EDGE",EDGE,{"disambiguationData":[OSD([sQuery(id+"F8.wireOp",EDGE,"E17.bottom")])],"isStart":false})});
            fillet(context, id + "F23", {"entities" : qUnion([Q0, Q1, Q2, Q3, Q4, Q5, Q6, Q7, Q8, Q9, Q10, Q11, Q12]), "radius" : 2 * mm, "tangentPropagation" : true, "allowEdgeOverflow" : false});
        }
        {
            var Q0;
            Q0=makeQuery(id+"F6.imprint","IMPRINT",FACE,{"disambiguationData":[TD([[makeQuery(id+"F6.imprint","IMPRINT",EDGE,{"derivedFrom":sQuery(id+"F6.wireOp",EDGE,"E15")}),1.0]])]});
            extrude(context, id + "F24", {"entities" : qUnion([Q0]), "operationType" : NewBodyOperationType.REMOVE, "endBound" : BoundingType.UP_TO_NEXT, "oppositeDirection" : true, "depth" : 25 * mm, "offsetDistance" : 25 * mm});
        }
        {
            var Q0;
            Q0=makeQuery(id+"F1.opExtrude","CAP_FACE",FACE,{"disambiguationData":[OSD([sQuery(id+"F0.wireOp",EDGE,"E0.bottom"),sQuery(id+"F0.wireOp",EDGE,"E0.top"),sQuery(id+"F0.wireOp",EDGE,"E0.left"),sQuery(id+"F0.wireOp",EDGE,"E0.right"),sQuery(id+"F0.wireOp",EDGE,"E1"),sQuery(id+"F0.wireOp",EDGE,"E2"),sQuery(id+"F0.wireOp",EDGE,"E3"),sQuery(id+"F0.wireOp",EDGE,"E4")])],"isStart":true});
            var sketch = newSketch(context, id + "F25", { "sketchPlane" : qUnion([Q0])});
            skLineSegment(sketch, "E50.bottom", {"start": v(9.55, -21.7) * mm, "end": v(15.55, -21.7) * mm});
            skLineSegment(sketch, "E50.top", {"start": v(9.55, -26.7) * mm, "end": v(15.55, -26.7) * mm});
            skLineSegment(sketch, "E50.left", {"start": v(9.55, -21.7) * mm, "end": v(9.55, -26.7) * mm});
            skLineSegment(sketch, "E50.right", {"start": v(15.55, -21.7) * mm, "end": v(15.55, -26.7) * mm});
            skPoint(sketch, "E51", {"position": v(9.55, -24.2) * mm});
            skSolve(sketch);
        }
        {
            var Q0;
            Q0=makeQuery(id+"F25.imprint","IMPRINT",FACE,{"disambiguationData":[TD([[makeQuery(id+"F25.imprint","IMPRINT",EDGE,{"derivedFrom":sQuery(id+"F25.wireOp",EDGE,"E50.bottom")}),-1.0]])]});
            extrude(context, id + "F26", {"entities" : qUnion([Q0]), "operationType" : NewBodyOperationType.REMOVE, "oppositeDirection" : true, "depth" : 3 * mm, "offsetDistance" : 25 * mm});
        }
        {
            var Q0;
            Q0=makeQuery(id+"F6.imprint","IMPRINT",FACE,{"disambiguationData":[TD([[makeQuery(id+"F6.imprint","IMPRINT",EDGE,{"derivedFrom":sQuery(id+"F6.wireOp",EDGE,"E15")}),-1.0]])]});
            var sketch = newSketch(context, id + "F27", { "sketchPlane" : qUnion([Q0])});
            skLineSegment(sketch, "E52.0.0", {"start": v(15.55, 35) * mm, "end": v(9.55, 35) * mm, "construction": true});
            skLineSegment(sketch, "E52.0.1", {"start": v(9.55, 35) * mm, "end": v(9.55, -7) * mm, "construction": true});
            skLineSegment(sketch, "E52.0.2", {"start": v(9.55, -7) * mm, "end": v(-40.25, -7) * mm, "construction": true});
            skLineSegment(sketch, "E52.0.3", {"start": v(-40.25, -7) * mm, "end": v(-40.25, -15) * mm, "construction": true});
            skLineSegment(sketch, "E52.0.4", {"start": v(-40.25, -15) * mm, "end": v(9.55, -15) * mm, "construction": true});
            skLineSegment(sketch, "E52.0.5", {"start": v(9.55, -15) * mm, "end": v(9.55, -35) * mm, "construction": true});
            skLineSegment(sketch, "E52.0.6", {"start": v(9.55, -35) * mm, "end": v(15.55, -35) * mm, "construction": true});
            skLineSegment(sketch, "E52.0.7", {"start": v(15.55, -35) * mm, "end": v(15.55, -15) * mm, "construction": true});
            skLineSegment(sketch, "E52.0.8", {"start": v(15.55, -15) * mm, "end": v(40.25, -15) * mm, "construction": true});
            skLineSegment(sketch, "E52.0.9", {"start": v(40.25, -15) * mm, "end": v(40.25, -7) * mm, "construction": true});
            skLineSegment(sketch, "E52.0.10", {"start": v(40.25, -7) * mm, "end": v(15.55, -7) * mm, "construction": true});
            skLineSegment(sketch, "E52.0.11", {"start": v(15.55, -7) * mm, "end": v(15.55, 35) * mm, "construction": true});
            skLineSegment(sketch, "E53.bottom", {"start": v(40.25, -7) * mm, "end": v(35.25, -7) * mm});
            skLineSegment(sketch, "E53.top", {"start": v(40.25, -15) * mm, "end": v(35.25, -15) * mm});
            skLineSegment(sketch, "E53.left", {"start": v(40.25, -7) * mm, "end": v(40.25, -15) * mm});
            skLineSegment(sketch, "E53.right", {"start": v(35.25, -7) * mm, "end": v(35.25, -15) * mm});
            skSolve(sketch);
        }
        {
            var Q0;
            Q0=makeQuery(id+"F27.imprint","IMPRINT",FACE,{"disambiguationData":[TD([[makeQuery(id+"F27.imprint","IMPRINT",EDGE,{"derivedFrom":sQuery(id+"F27.wireOp",EDGE,"E53.bottom")}),-1.0]])]});
            var Q1;
            Q1=makeQuery(id+"F13.boolean.opBoolean","COPY",FACE,{"derivedFrom":makeQuery(id+"F13.opExtrude","CAP_FACE",FACE,{"disambiguationData":[OSD([sQuery(id+"F12.wireOp",EDGE,"E42.bottom"),sQuery(id+"F12.wireOp",EDGE,"E42.top"),sQuery(id+"F12.wireOp",EDGE,"E42.left"),sQuery(id+"F12.wireOp",EDGE,"E42.right")])],"isStart":false})});
            extrude(context, id + "F28", {"entities" : qUnion([Q0]), "operationType" : NewBodyOperationType.ADD, "endBound" : BoundingType.UP_TO_SURFACE, "depth" : 25 * mm, "endBoundEntityFace" : qUnion([Q1]), "offsetDistance" : 25 * mm});
        }
    });
